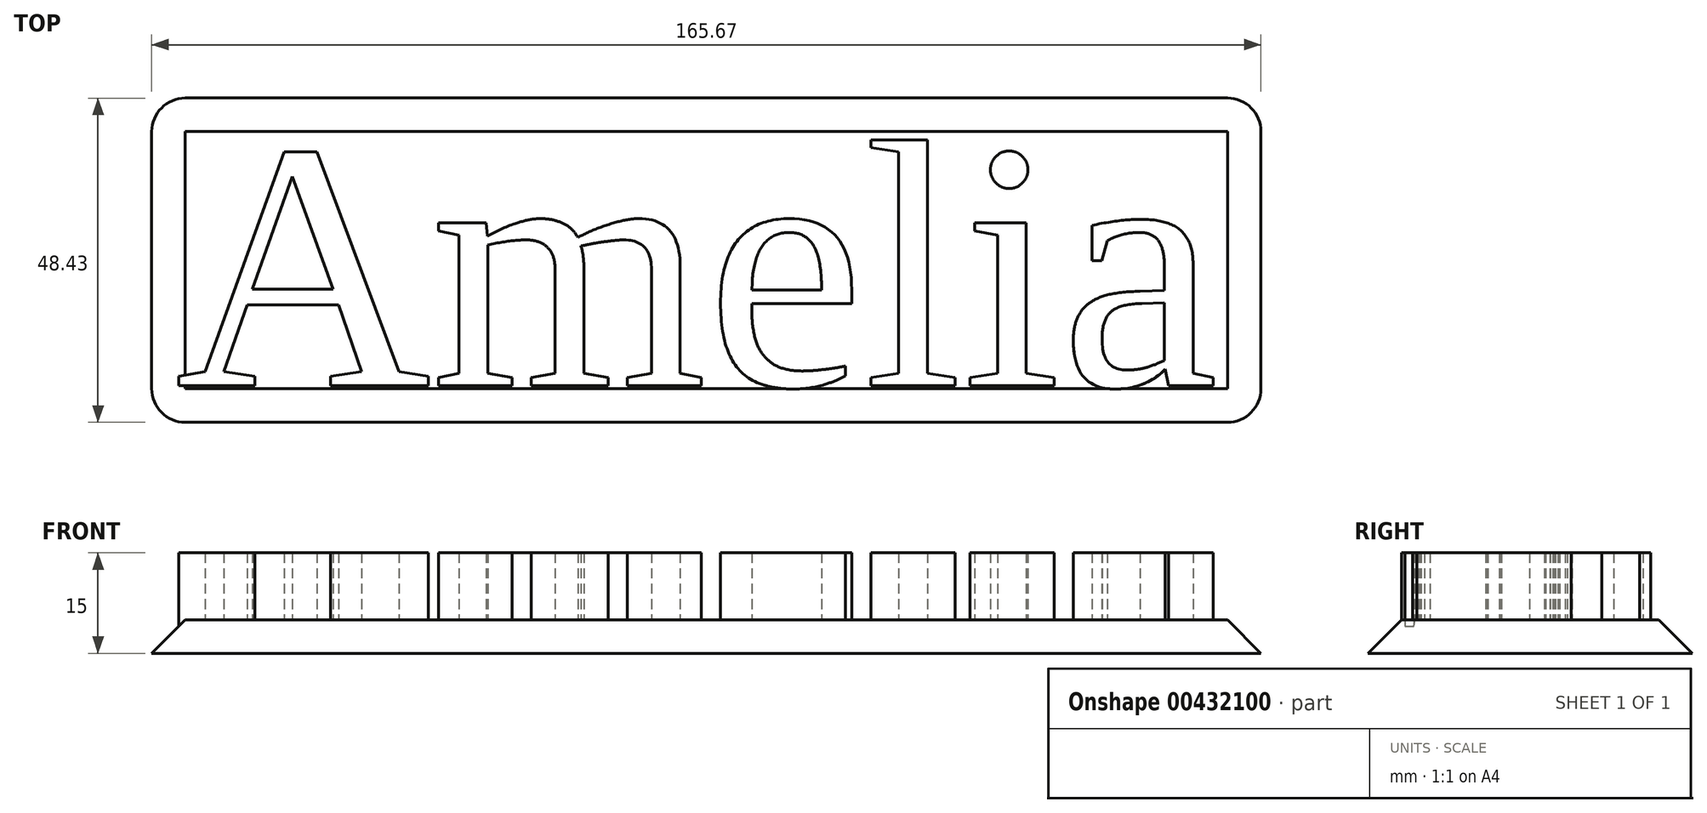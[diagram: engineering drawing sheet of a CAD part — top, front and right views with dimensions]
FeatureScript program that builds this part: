
annotation { "Feature Type Name" : "Feature", "Feature Type Description" : "" }
export const myFeature = defineFeature(function(context is Context, id is Id, definition is map)
    precondition{}
    {
        {
            var Q0;
            Q0=qCreatedBy(makeId("Top.planeOp"),FACE);
            var sketch = newSketch(context, id + "F0", { "sketchPlane" : qUnion([Q0])});
            skLineSegment(sketch, "E0.bottom", {"start": v(-76.92, 23.61) * mm, "end": v(88.9, 23.61) * mm});
            skLineSegment(sketch, "E0.top", {"start": v(-76.92, -24.98) * mm, "end": v(88.9, -24.98) * mm});
            skLineSegment(sketch, "E0.left", {"start": v(-76.92, 23.61) * mm, "end": v(-76.92, -24.98) * mm});
            skLineSegment(sketch, "E0.right", {"start": v(88.9, 23.61) * mm, "end": v(88.9, -24.98) * mm});
            skText(sketch, "E1", { "text": "Amelia", "fontName": "Tinos-Regular.ttf"});
            const initialGuessF0  = {"E1": [-0.07333, -0.01941, 1, 0, 0.0381]};
            skSetInitialGuess(sketch, initialGuessF0);
            skSolve(sketch);
        }
        {
            var Q0;
            Q0=makeQuery(id+"F0.imprint","IMPRINT",FACE,{"disambiguationData":[TD([[makeQuery(id+"F0.imprint","IMPRINT",EDGE,{"derivedFrom":sQuery(id+"F0.wireOp",EDGE,"E1.sketch_text.stroke-60")}),-1.0]])]});
            var Q1;
            Q1=makeQuery(id+"F0.imprint","IMPRINT",FACE,{"disambiguationData":[TD([[makeQuery(id+"F0.imprint","IMPRINT",EDGE,{"derivedFrom":sQuery(id+"F0.wireOp",EDGE,"E1.sketch_text.stroke-76")}),1.0]])]});
            var Q2;
            Q2=makeQuery(id+"F0.imprint","IMPRINT",FACE,{"disambiguationData":[TD([[makeQuery(id+"F0.imprint","IMPRINT",EDGE,{"derivedFrom":sQuery(id+"F0.wireOp",EDGE,"E1.sketch_text.stroke-81")}),-1.0]])]});
            var Q3;
            Q3=makeQuery(id+"F0.imprint","IMPRINT",FACE,{"disambiguationData":[TD([[makeQuery(id+"F0.imprint","IMPRINT",EDGE,{"derivedFrom":sQuery(id+"F0.wireOp",EDGE,"E0.bottom")}),-1.0]])]});
            var Q4;
            Q4=makeQuery(id+"F0.imprint","IMPRINT",FACE,{"disambiguationData":[TD([[makeQuery(id+"F0.imprint","IMPRINT",EDGE,{"derivedFrom":sQuery(id+"F0.wireOp",EDGE,"E1.sketch_text.stroke-109")}),-1.0]])]});
            var Q5;
            Q5=makeQuery(id+"F0.imprint","IMPRINT",FACE,{"disambiguationData":[TD([[makeQuery(id+"F0.imprint","IMPRINT",EDGE,{"derivedFrom":sQuery(id+"F0.wireOp",EDGE,"E1.sketch_text.stroke-0")}),-1.0]])]});
            var Q6;
            Q6=makeQuery(id+"F0.imprint","IMPRINT",FACE,{"disambiguationData":[TD([[makeQuery(id+"F0.imprint","IMPRINT",EDGE,{"derivedFrom":sQuery(id+"F0.wireOp",EDGE,"E1.sketch_text.stroke-130")}),1.0]])]});
            var Q7;
            Q7=makeQuery(id+"F0.imprint","IMPRINT",FACE,{"disambiguationData":[TD([[makeQuery(id+"F0.imprint","IMPRINT",EDGE,{"derivedFrom":sQuery(id+"F0.wireOp",EDGE,"E1.sketch_text.stroke-16")}),1.0]])]});
            var Q8;
            Q8=makeQuery(id+"F0.imprint","IMPRINT",FACE,{"disambiguationData":[TD([[makeQuery(id+"F0.imprint","IMPRINT",EDGE,{"derivedFrom":sQuery(id+"F0.wireOp",EDGE,"E1.sketch_text.stroke-99")}),-1.0]])]});
            var Q9;
            Q9=makeQuery(id+"F0.imprint","IMPRINT",FACE,{"disambiguationData":[TD([[makeQuery(id+"F0.imprint","IMPRINT",EDGE,{"derivedFrom":sQuery(id+"F0.wireOp",EDGE,"E1.sketch_text.stroke-91")}),-1.0]])]});
            var Q10;
            Q10=makeQuery(id+"F0.imprint","IMPRINT",FACE,{"disambiguationData":[TD([[makeQuery(id+"F0.imprint","IMPRINT",EDGE,{"derivedFrom":sQuery(id+"F0.wireOp",EDGE,"E1.sketch_text.stroke-19")}),-1.0]])]});
            extrude(context, id + "F1", {"entities" : qUnion([Q0, Q1, Q2, Q3, Q4, Q5, Q6, Q7, Q8, Q9, Q10]), "oppositeDirection" : true, "depth" : 5 * mm});
        }
        {
            var Q0;
            Q0=makeQuery(id+"F0.imprint","IMPRINT",FACE,{"disambiguationData":[TD([[makeQuery(id+"F0.imprint","IMPRINT",EDGE,{"derivedFrom":sQuery(id+"F0.wireOp",EDGE,"E1.sketch_text.stroke-0")}),-1.0]])]});
            var Q1;
            Q1=makeQuery(id+"F0.imprint","IMPRINT",FACE,{"disambiguationData":[TD([[makeQuery(id+"F0.imprint","IMPRINT",EDGE,{"derivedFrom":sQuery(id+"F0.wireOp",EDGE,"E1.sketch_text.stroke-19")}),-1.0]])]});
            var Q2;
            Q2=makeQuery(id+"F0.imprint","IMPRINT",FACE,{"disambiguationData":[TD([[makeQuery(id+"F0.imprint","IMPRINT",EDGE,{"derivedFrom":sQuery(id+"F0.wireOp",EDGE,"E1.sketch_text.stroke-60")}),-1.0]])]});
            var Q3;
            Q3=makeQuery(id+"F0.imprint","IMPRINT",FACE,{"disambiguationData":[TD([[makeQuery(id+"F0.imprint","IMPRINT",EDGE,{"derivedFrom":sQuery(id+"F0.wireOp",EDGE,"E1.sketch_text.stroke-81")}),-1.0]])]});
            var Q4;
            Q4=makeQuery(id+"F0.imprint","IMPRINT",FACE,{"disambiguationData":[TD([[makeQuery(id+"F0.imprint","IMPRINT",EDGE,{"derivedFrom":sQuery(id+"F0.wireOp",EDGE,"E1.sketch_text.stroke-99")}),-1.0]])]});
            var Q5;
            Q5=makeQuery(id+"F0.imprint","IMPRINT",FACE,{"disambiguationData":[TD([[makeQuery(id+"F0.imprint","IMPRINT",EDGE,{"derivedFrom":sQuery(id+"F0.wireOp",EDGE,"E1.sketch_text.stroke-109")}),-1.0]])]});
            var Q6;
            Q6=makeQuery(id+"F0.imprint","IMPRINT",FACE,{"disambiguationData":[TD([[makeQuery(id+"F0.imprint","IMPRINT",EDGE,{"derivedFrom":sQuery(id+"F0.wireOp",EDGE,"E1.sketch_text.stroke-91")}),-1.0]])]});
            extrude(context, id + "F2", {"entities" : qUnion([Q0, Q1, Q2, Q3, Q4, Q5, Q6]), "operationType" : NewBodyOperationType.ADD, "depth" : 10 * mm});
        }
        {
            var Q0;
            Q0=makeQuery(id+"F1.opExtrude","SWEPT_EDGE",EDGE,{"disambiguationData":[OSD([sQuery(id+"F0.wireOp",EDGE,"E0.bottom"),sQuery(id+"F0.wireOp",EDGE,"E0.left")])]});
            var Q1;
            Q1=makeQuery(id+"F1.opExtrude","SWEPT_EDGE",EDGE,{"disambiguationData":[OSD([sQuery(id+"F0.wireOp",EDGE,"E0.top"),sQuery(id+"F0.wireOp",EDGE,"E0.right")])]});
            var Q2;
            Q2=makeQuery(id+"F1.opExtrude","SWEPT_EDGE",EDGE,{"disambiguationData":[OSD([sQuery(id+"F0.wireOp",EDGE,"E0.bottom"),sQuery(id+"F0.wireOp",EDGE,"E0.right")])]});
            fillet(context, id + "F3", {"entities" : qUnion([Q0, Q1, Q2]), "radius" : 5.08 * mm, "tangentPropagation" : true, "allowEdgeOverflow" : false});
        }
        {
            var Q0;
            Q0=makeQuery(id+"F1.opExtrude","SWEPT_EDGE",EDGE,{"disambiguationData":[OSD([sQuery(id+"F0.wireOp",EDGE,"E0.top"),sQuery(id+"F0.wireOp",EDGE,"E0.left")])]});
            fillet(context, id + "F4", {"entities" : qUnion([Q0]), "radius" : 5.08 * mm, "tangentPropagation" : true, "allowEdgeOverflow" : false});
        }
        {
            var Q0;
            {var subQ0=sQuery(id+"F0.wireOp",EDGE,"E0.left");var subQ1=sQuery(id+"F0.wireOp",EDGE,"E0.top");var subQ2=sQuery(id+"F0.wireOp",EDGE,"E0.right");var subQ3=sQuery(id+"F0.wireOp",EDGE,"E0.bottom");Q0=makeQuery(id+"F4.opFillet","BLEND_EDGE",EDGE,{"blendedFrom":[makeQuery(id+"F1.opExtrude","SWEPT_EDGE",EDGE,{"disambiguationData":[OSD([subQ1,subQ0])]}),makeQuery(id+"F2.boolean.opBoolean","SPLIT",FACE,{"disambiguationData":[TD([makeQuery(id+"F1.opExtrude","SWEPT_FACE",FACE,{"disambiguationData":[OSD([subQ3])]})])],"derivedFrom":makeQuery(id+"F1.opExtrude","CAP_FACE",FACE,{"disambiguationData":[OSD([subQ3,subQ1,subQ0,subQ2])],"isStart":true})})],"blendedInto":[makeQuery(id+"F2.boolean.opBoolean","SPLIT",FACE,{"disambiguationData":[TD([makeQuery(id+"F1.opExtrude","SWEPT_FACE",FACE,{"disambiguationData":[OSD([subQ3])]})])],"derivedFrom":makeQuery(id+"F1.opExtrude","CAP_FACE",FACE,{"disambiguationData":[OSD([subQ3,subQ1,subQ0,subQ2])],"isStart":true})})]});}
            var Q1;
            {var subQ0=sQuery(id+"F0.wireOp",EDGE,"E0.left");var subQ1=sQuery(id+"F0.wireOp",EDGE,"E0.top");var subQ2=sQuery(id+"F0.wireOp",EDGE,"E0.right");var subQ3=sQuery(id+"F0.wireOp",EDGE,"E0.bottom");Q1=makeQuery(id+"F3.opFillet","BLEND_EDGE",EDGE,{"blendedFrom":[makeQuery(id+"F1.opExtrude","SWEPT_EDGE",EDGE,{"disambiguationData":[OSD([subQ1,subQ2])]}),makeQuery(id+"F2.boolean.opBoolean","SPLIT",FACE,{"disambiguationData":[TD([makeQuery(id+"F1.opExtrude","SWEPT_FACE",FACE,{"disambiguationData":[OSD([subQ3])]})])],"derivedFrom":makeQuery(id+"F1.opExtrude","CAP_FACE",FACE,{"disambiguationData":[OSD([subQ3,subQ1,subQ0,subQ2])],"isStart":true})})],"blendedInto":[makeQuery(id+"F2.boolean.opBoolean","SPLIT",FACE,{"disambiguationData":[TD([makeQuery(id+"F1.opExtrude","SWEPT_FACE",FACE,{"disambiguationData":[OSD([subQ3])]})])],"derivedFrom":makeQuery(id+"F1.opExtrude","CAP_FACE",FACE,{"disambiguationData":[OSD([subQ3,subQ1,subQ0,subQ2])],"isStart":true})})]});}
            var Q2;
            {var subQ0=sQuery(id+"F0.wireOp",EDGE,"E0.left");var subQ1=sQuery(id+"F0.wireOp",EDGE,"E0.top");var subQ2=sQuery(id+"F0.wireOp",EDGE,"E0.right");var subQ3=sQuery(id+"F0.wireOp",EDGE,"E0.bottom");Q2=makeQuery(id+"F3.opFillet","BLEND_EDGE",EDGE,{"blendedFrom":[makeQuery(id+"F1.opExtrude","SWEPT_EDGE",EDGE,{"disambiguationData":[OSD([subQ3,subQ2])]}),makeQuery(id+"F2.boolean.opBoolean","SPLIT",FACE,{"disambiguationData":[TD([makeQuery(id+"F1.opExtrude","SWEPT_FACE",FACE,{"disambiguationData":[OSD([subQ3])]})])],"derivedFrom":makeQuery(id+"F1.opExtrude","CAP_FACE",FACE,{"disambiguationData":[OSD([subQ3,subQ1,subQ0,subQ2])],"isStart":true})})],"blendedInto":[makeQuery(id+"F2.boolean.opBoolean","SPLIT",FACE,{"disambiguationData":[TD([makeQuery(id+"F1.opExtrude","SWEPT_FACE",FACE,{"disambiguationData":[OSD([subQ3])]})])],"derivedFrom":makeQuery(id+"F1.opExtrude","CAP_FACE",FACE,{"disambiguationData":[OSD([subQ3,subQ1,subQ0,subQ2])],"isStart":true})})]});}
            var Q3;
            {var subQ0=sQuery(id+"F0.wireOp",EDGE,"E0.left");var subQ1=sQuery(id+"F0.wireOp",EDGE,"E0.top");var subQ2=sQuery(id+"F0.wireOp",EDGE,"E0.right");var subQ3=sQuery(id+"F0.wireOp",EDGE,"E0.bottom");Q3=makeQuery(id+"F3.opFillet","BLEND_EDGE",EDGE,{"blendedFrom":[makeQuery(id+"F1.opExtrude","SWEPT_EDGE",EDGE,{"disambiguationData":[OSD([subQ3,subQ0])]}),makeQuery(id+"F2.boolean.opBoolean","SPLIT",FACE,{"disambiguationData":[TD([makeQuery(id+"F1.opExtrude","SWEPT_FACE",FACE,{"disambiguationData":[OSD([subQ3])]})])],"derivedFrom":makeQuery(id+"F1.opExtrude","CAP_FACE",FACE,{"disambiguationData":[OSD([subQ3,subQ1,subQ0,subQ2])],"isStart":true})})],"blendedInto":[makeQuery(id+"F2.boolean.opBoolean","SPLIT",FACE,{"disambiguationData":[TD([makeQuery(id+"F1.opExtrude","SWEPT_FACE",FACE,{"disambiguationData":[OSD([subQ3])]})])],"derivedFrom":makeQuery(id+"F1.opExtrude","CAP_FACE",FACE,{"disambiguationData":[OSD([subQ3,subQ1,subQ0,subQ2])],"isStart":true})})]});}
            var Q4;
            Q4=makeQuery(id+"F1.opExtrude","CAP_EDGE",EDGE,{"disambiguationData":[OSD([sQuery(id+"F0.wireOp",EDGE,"E0.bottom")])],"isStart":true});
            var Q5;
            Q5=makeQuery(id+"F1.opExtrude","CAP_EDGE",EDGE,{"disambiguationData":[OSD([sQuery(id+"F0.wireOp",EDGE,"E0.top")])],"isStart":true});
            var Q6;
            Q6=makeQuery(id+"F1.opExtrude","CAP_EDGE",EDGE,{"disambiguationData":[OSD([sQuery(id+"F0.wireOp",EDGE,"E0.right")])],"isStart":true});
            var Q7;
            Q7=makeQuery(id+"F1.opExtrude","CAP_EDGE",EDGE,{"disambiguationData":[OSD([sQuery(id+"F0.wireOp",EDGE,"E0.left")])],"isStart":true});
            chamfer(context, id + "F5", {"entities" : qUnion([Q0, Q1, Q2, Q3, Q4, Q5, Q6, Q7]), "width" : 5.08 * mm, "tangentPropagation" : true});
        }
    });
